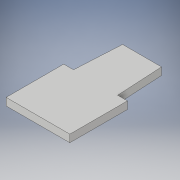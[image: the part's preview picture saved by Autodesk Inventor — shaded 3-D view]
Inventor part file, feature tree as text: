
AUTODESK INVENTOR PART (.ipt)
format: ipt  version: 2018 (Build 220112000, 112)  size: 97,792 bytes
history: native  units: in
note: dims shown in document units (in); Inventor stores cm internally (conversion verified against a paired STEP export)
features: extrude x1, sketch x1
ambient origin geometry x8: Origin, YZ Plane, XZ Plane, XY Plane, X Axis, Y Axis, Z Axis, Center Point
bodies: Body1 (feature_tree)
feature tree (2):
  extrude  "Extrusion2"  Depth=0.2756in TaperAngle=0.0deg
  sketch  "Sketch1"  dims[d4=3.8583in d5=0.2756in d6=0.0in d7=1.1811in]
